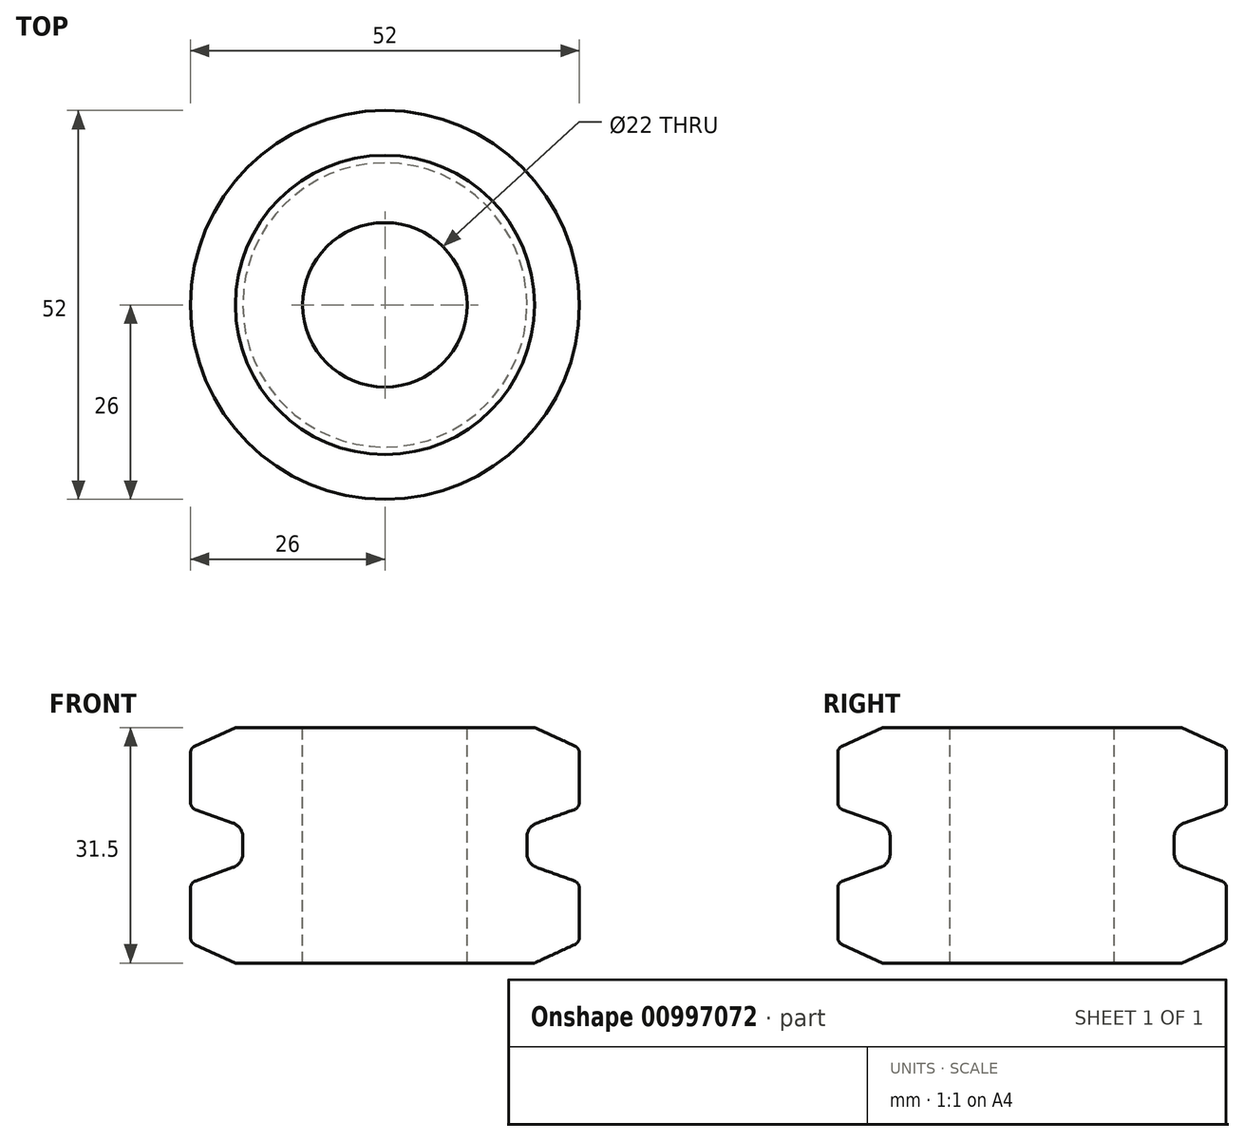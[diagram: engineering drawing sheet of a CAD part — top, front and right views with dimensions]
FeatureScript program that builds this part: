
annotation { "Feature Type Name" : "Feature", "Feature Type Description" : "" }
export const myFeature = defineFeature(function(context is Context, id is Id, definition is map)
    precondition{}
    {
        {
            var Q0;
            Q0=qCreatedBy(makeId("Right.planeOp"),FACE);
            var sketch = newSketch(context, id + "F0", { "sketchPlane" : qUnion([Q0])});
            skLineSegment(sketch, "E0", {"start": v(0, 0) * mm, "end": v(11, 0) * mm, "construction": true});
            skLineSegment(sketch, "E1", {"start": v(11, 15.75) * mm, "end": v(11, -15.75) * mm});
            skLineSegment(sketch, "E2", {"start": v(11, 15.75) * mm, "end": v(20, 15.75) * mm});
            skLineSegment(sketch, "E3", {"start": v(0, 13) * mm, "end": v(26, 13) * mm, "construction": true});
            skLineSegment(sketch, "E4", {"start": v(26, 12.36) * mm, "end": v(26, 5.7) * mm});
            skLineSegment(sketch, "E5", {"start": v(0, 0) * mm, "end": v(19, 0) * mm, "construction": true});
            skLineSegment(sketch, "E6", {"start": v(19, 0) * mm, "end": v(19, 1.1) * mm});
            skLineSegment(sketch, "E7", {"start": v(20.33, 2.97) * mm, "end": v(25.34, 4.76) * mm});
            skLineSegment(sketch, "E8", {"start": v(20, 15.75) * mm, "end": v(25.42, 13.27) * mm});
            skPoint(sketch, "E9.visualSharp", {"position": v(19, 2.5) * mm});
            skArc(sketch, "E9.filletArc", {"start": v(20.33, 2.97) * mm, "mid": v(19.37, 2.24) * mm, "end": v(19, 1.1) * mm});
            skPoint(sketch, "E10.visualSharp", {"position": v(26, 5) * mm});
            skArc(sketch, "E10.filletArc", {"start": v(25.34, 4.76) * mm, "mid": v(25.82, 5.13) * mm, "end": v(26, 5.7) * mm});
            skPoint(sketch, "E11.visualSharp", {"position": v(26, 13) * mm});
            skArc(sketch, "E11.filletArc", {"start": v(26, 12.36) * mm, "mid": v(25.84, 12.9) * mm, "end": v(25.42, 13.27) * mm});
            skArc(sketch, "E12.MirrorCS", {"start": v(26, -12.36) * mm, "mid": v(25.84, -12.9) * mm, "end": v(25.42, -13.27) * mm});
            skArc(sketch, "E13.MirrorCS", {"start": v(25.34, -4.76) * mm, "mid": v(25.82, -5.13) * mm, "end": v(26, -5.7) * mm});
            skLineSegment(sketch, "E14.MirrorCS", {"start": v(26, -12.36) * mm, "end": v(26, -5.7) * mm});
            skLineSegment(sketch, "E15.MirrorCS", {"start": v(11, -15.75) * mm, "end": v(20, -15.75) * mm});
            skPoint(sketch, "E16.MirrorP", {"position": v(26, -13) * mm});
            skLineSegment(sketch, "E17.MirrorCS", {"start": v(19, 0) * mm, "end": v(19, -1.1) * mm});
            skPoint(sketch, "E18.MirrorP", {"position": v(19, -2.5) * mm});
            skLineSegment(sketch, "E19.MirrorCS", {"start": v(20, -15.75) * mm, "end": v(25.42, -13.27) * mm});
            skLineSegment(sketch, "E20.MirrorCS", {"start": v(20.33, -2.97) * mm, "end": v(25.34, -4.76) * mm});
            skPoint(sketch, "E21.MirrorP", {"position": v(26, -5) * mm});
            skArc(sketch, "E22.MirrorCS", {"start": v(20.33, -2.97) * mm, "mid": v(19.37, -2.24) * mm, "end": v(19, -1.1) * mm});
            skLineSegment(sketch, "E23", {"start": v(0, 23.98) * mm, "end": v(0, -22.1) * mm, "construction": true});
            skSolve(sketch);
        }
        {
            var Q0;
            Q0=makeQuery(id+"F0.imprint","IMPRINT",FACE,{"disambiguationData":[TD([[makeQuery(id+"F0.imprint","IMPRINT",EDGE,{"derivedFrom":sQuery(id+"F0.wireOp",EDGE,"E1")}),1.0]])]});
            var Q1;
            Q1=sQuery(id+"F0.wireOp",EDGE,"E23");
            revolve(context, id + "F1", {"surfaceOperationType" : NewSurfaceOperationType.NEW, "entities" : qUnion([Q0]), "axis" : qUnion([Q1]), "revolveType" : RevolveType.FULL});
        }
    });
